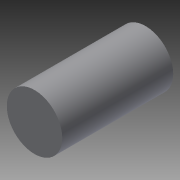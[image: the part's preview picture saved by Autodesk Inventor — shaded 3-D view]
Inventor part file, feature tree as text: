
AUTODESK INVENTOR PART (.ipt)
format: ipt  version: 2014 (Build 180170000, 170)  size: 71,680 bytes
history: native  units: in
note: dims shown in document units (in); Inventor stores cm internally (conversion verified against a paired STEP export)
features: extrude x1, sketch x1
ambient origin geometry x8: Origin, YZ Plane, XZ Plane, XY Plane, X Axis, Y Axis, Z Axis, Center Point
bodies: Solid1 (feature_tree)
feature tree (2):
  extrude  "Extrusion1"  Depth=0.5in TaperAngle=0.0deg
  sketch  "Sketch1"  dims[d0=0.25in d1=0.5in d2=0.0in]
